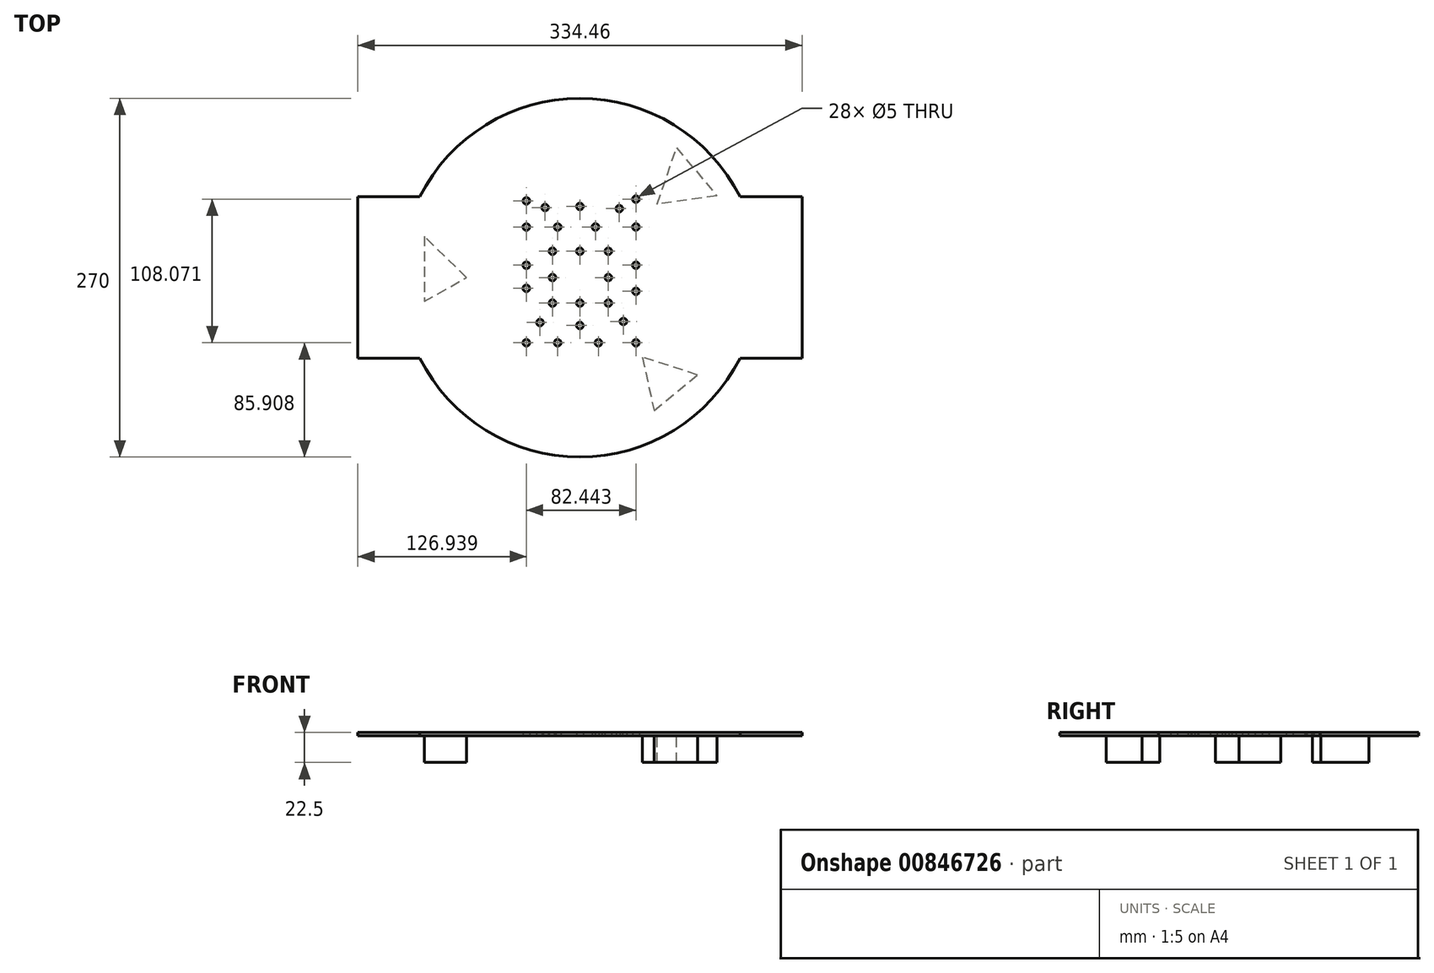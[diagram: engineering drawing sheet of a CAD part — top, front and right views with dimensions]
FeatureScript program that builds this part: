
annotation { "Feature Type Name" : "Feature", "Feature Type Description" : "" }
export const myFeature = defineFeature(function(context is Context, id is Id, definition is map)
    precondition{}
    {
        {
            var Q0;
            Q0=qCreatedBy(makeId("Top.planeOp"),FACE);
            var sketch = newSketch(context, id + "F0", { "sketchPlane" : qUnion([Q0])});
            skCircle(sketch, "E0", {"center": v(0, 0) * mm, "radius": 135 * mm});
            skLineSegment(sketch, "E1.left", {"start": v(167.23, 60.8) * mm, "end": v(167.23, -60.8) * mm});
            skLineSegment(sketch, "E1.right", {"start": v(-167.23, 60.8) * mm, "end": v(-167.23, -60.8) * mm});
            skLineSegment(sketch, "E2", {"start": v(-167.23, 60.8) * mm, "end": v(-120.53, 60.8) * mm});
            skLineSegment(sketch, "E3", {"start": v(120.53, 60.8) * mm, "end": v(167.23, 60.8) * mm});
            skLineSegment(sketch, "E4", {"start": v(-167.23, -60.8) * mm, "end": v(-120.53, -60.8) * mm});
            skLineSegment(sketch, "E5", {"start": v(120.53, -60.8) * mm, "end": v(167.23, -60.8) * mm});
            skPoint(sketch, "E6", {"position": v(0, 19.8) * mm});
            skPoint(sketch, "E7", {"position": v(0, -19.21) * mm});
            skPoint(sketch, "E8", {"position": v(21.4, 0) * mm});
            skPoint(sketch, "E9", {"position": v(-20.65, 0) * mm});
            skPoint(sketch, "E10", {"position": v(-20.65, 19.8) * mm});
            skPoint(sketch, "E11", {"position": v(21.4, 19.8) * mm});
            skPoint(sketch, "E12", {"position": v(21.4, -19.21) * mm});
            skPoint(sketch, "E13", {"position": v(-20.65, -19.21) * mm});
            skPoint(sketch, "E14", {"position": v(-16.78, -49.1) * mm});
            skPoint(sketch, "E15", {"position": v(13.93, -49.1) * mm});
            skPoint(sketch, "E16", {"position": v(11.72, 38.05) * mm});
            skPoint(sketch, "E17", {"position": v(-16.78, 38.05) * mm});
            skPoint(sketch, "E18", {"position": v(42.15, 9.28) * mm});
            skPoint(sketch, "E19", {"position": v(42.15, -10.36) * mm});
            skPoint(sketch, "E20", {"position": v(-40.3, -8.15) * mm});
            skPoint(sketch, "E21", {"position": v(-40.3, 9.28) * mm});
            skPoint(sketch, "E22", {"position": v(-40.3, 38.05) * mm});
            skPoint(sketch, "E23", {"position": v(42.15, 38.05) * mm});
            skPoint(sketch, "E24", {"position": v(42.15, -49.1) * mm});
            skPoint(sketch, "E25", {"position": v(-40.3, -49.1) * mm});
            skPoint(sketch, "E26", {"position": v(0, -36.09) * mm});
            skPoint(sketch, "E27", {"position": v(-30.05, -33.88) * mm});
            skPoint(sketch, "E28", {"position": v(32.75, -33.05) * mm});
            skPoint(sketch, "E29", {"position": v(-26.18, 52.72) * mm});
            skPoint(sketch, "E30", {"position": v(0, 53.55) * mm});
            skPoint(sketch, "E31", {"position": v(29.7, 51.89) * mm});
            skPoint(sketch, "E32", {"position": v(-40.3, 57.7) * mm});
            skPoint(sketch, "E33", {"position": v(42.15, 58.98) * mm});
            skLineSegment(sketch, "E34", {"start": v(-117.25, 31.13) * mm, "end": v(-117.25, -17.96) * mm});
            skLineSegment(sketch, "E35", {"start": v(-117.25, -17.96) * mm, "end": v(-85.33, 0) * mm});
            skLineSegment(sketch, "E36", {"start": v(-85.33, 0) * mm, "end": v(-117.25, 31.13) * mm});
            skLineSegment(sketch, "E37", {"start": v(72.76, 97.7) * mm, "end": v(103.14, 61.47) * mm});
            skLineSegment(sketch, "E38", {"start": v(103.14, 61.47) * mm, "end": v(58.2, 55.23) * mm});
            skLineSegment(sketch, "E39", {"start": v(58.2, 55.23) * mm, "end": v(72.76, 97.7) * mm});
            skLineSegment(sketch, "E40", {"start": v(55.9, -100.06) * mm, "end": v(88.54, -73.28) * mm});
            skLineSegment(sketch, "E41", {"start": v(88.54, -73.28) * mm, "end": v(46.94, -59.96) * mm});
            skLineSegment(sketch, "E42", {"start": v(46.94, -59.96) * mm, "end": v(55.9, -100.06) * mm});
            skSolve(sketch);
        }
        {
            var Q0;
            {var subQ0=sQuery(id+"F0.wireOp",EDGE,"E0");var subQ1=makeQuery(id+"F0.imprint","INTERSECT",VERTEX,{"derivedFrom":[subQ0,sQuery(id+"F0.wireOp",EDGE,"E2")]});Q0=makeQuery(id+"F0.imprint","IMPRINT",FACE,{"disambiguationData":[TD([[makeQuery(id+"F0.imprint","IMPRINT",EDGE,{"disambiguationData":[TD([[subQ1,1.0]])],"derivedFrom":subQ0}),1.0]])]});}
            var Q1;
            Q1=makeQuery(id+"F0.imprint","IMPRINT",FACE,{"disambiguationData":[TD([[makeQuery(id+"F0.imprint","IMPRINT",EDGE,{"derivedFrom":sQuery(id+"F0.wireOp",EDGE,"E1.right")}),1.0]])]});
            var Q2;
            Q2=makeQuery(id+"F0.imprint","IMPRINT",FACE,{"disambiguationData":[TD([[makeQuery(id+"F0.imprint","IMPRINT",EDGE,{"derivedFrom":sQuery(id+"F0.wireOp",EDGE,"E1.left")}),-1.0]])]});
            var Q3;
            {var subQ0=sQuery(id+"F0.wireOp",EDGE,"KSSbLjsO-GVq9-oAiS-ih5v-jaDQlpPfr1M6");Q3=makeQuery(id+"F0.imprint","IMPRINT",FACE,{"disambiguationData":[TD([[makeQuery(id+"F0.imprint","IMPRINT",EDGE,{"derivedFrom":subQ0}),-1.0]])]});}
            var Q4;
            {var subQ0=sQuery(id+"F0.wireOp",EDGE,"6y2jmlKQ-SfiU-YnZR-oIez-cIPMSW9u3y5p");Q4=makeQuery(id+"F0.imprint","IMPRINT",FACE,{"disambiguationData":[TD([[makeQuery(id+"F0.imprint","IMPRINT",EDGE,{"derivedFrom":subQ0}),1.0]])]});}
            var Q5;
            {var subQ0=sQuery(id+"F0.wireOp",EDGE,"5wtv1OCd-jvl7-qsIo-Mp1C-oISwUdbHLiSj");Q5=makeQuery(id+"F0.imprint","IMPRINT",FACE,{"disambiguationData":[TD([[makeQuery(id+"F0.imprint","IMPRINT",EDGE,{"derivedFrom":subQ0}),-1.0]])]});}
            var Q6;
            Q6=makeQuery(id+"F0.imprint","IMPRINT",FACE,{"disambiguationData":[TD([[makeQuery(id+"F0.imprint","IMPRINT",EDGE,{"derivedFrom":sQuery(id+"F0.wireOp",EDGE,"E34")}),1.0]])]});
            var Q7;
            Q7=makeQuery(id+"F0.imprint","IMPRINT",FACE,{"disambiguationData":[TD([[makeQuery(id+"F0.imprint","IMPRINT",EDGE,{"derivedFrom":sQuery(id+"F0.wireOp",EDGE,"E37")}),-1.0]])]});
            var Q8;
            Q8=makeQuery(id+"F0.imprint","IMPRINT",FACE,{"disambiguationData":[TD([[makeQuery(id+"F0.imprint","IMPRINT",EDGE,{"derivedFrom":sQuery(id+"F0.wireOp",EDGE,"E40")}),1.0]])]});
            extrude(context, id + "F1", {"entities" : qUnion([Q0, Q1, Q2, Q3, Q4, Q5, Q6, Q7, Q8]), "depth" : 2.5 * mm, "offsetDistance" : 25.4 * mm});
        }
        {
            var Q0;
            Q0=makeQuery(id+"F0.imprint","IMPRINT",FACE,{"disambiguationData":[TD([[makeQuery(id+"F0.imprint","IMPRINT",EDGE,{"derivedFrom":sQuery(id+"F0.wireOp",EDGE,"E34")}),1.0]])]});
            var Q1;
            Q1=makeQuery(id+"F0.imprint","IMPRINT",FACE,{"disambiguationData":[TD([[makeQuery(id+"F0.imprint","IMPRINT",EDGE,{"derivedFrom":sQuery(id+"F0.wireOp",EDGE,"E37")}),-1.0]])]});
            var Q2;
            Q2=makeQuery(id+"F0.imprint","IMPRINT",FACE,{"disambiguationData":[TD([[makeQuery(id+"F0.imprint","IMPRINT",EDGE,{"derivedFrom":sQuery(id+"F0.wireOp",EDGE,"E40")}),1.0]])]});
            extrude(context, id + "F2", {"entities" : qUnion([Q0, Q1, Q2]), "oppositeDirection" : true, "depth" : 20 * mm, "offsetDistance" : 25.4 * mm});
        }
        {
            var Q0;
            Q0=sQuery(id+"F0.wireOp",VERTEX,"E32");
            var Q1;
            Q1=sQuery(id+"F0.wireOp",VERTEX,"E22");
            var Q2;
            Q2=sQuery(id+"F0.wireOp",VERTEX,"E21");
            var Q3;
            Q3=sQuery(id+"F0.wireOp",VERTEX,"E20");
            var Q4;
            Q4=sQuery(id+"F0.wireOp",VERTEX,"E25");
            var Q5;
            Q5=sQuery(id+"F0.wireOp",VERTEX,"E27");
            var Q6;
            Q6=sQuery(id+"F0.wireOp",VERTEX,"E14");
            var Q7;
            Q7=sQuery(id+"F0.wireOp",VERTEX,"E13");
            var Q8;
            Q8=sQuery(id+"F0.wireOp",VERTEX,"E9");
            var Q9;
            Q9=sQuery(id+"F0.wireOp",VERTEX,"E10");
            var Q10;
            Q10=sQuery(id+"F0.wireOp",VERTEX,"E17");
            var Q11;
            Q11=sQuery(id+"F0.wireOp",VERTEX,"E29");
            var Q12;
            Q12=sQuery(id+"F0.wireOp",VERTEX,"E30");
            var Q13;
            Q13=sQuery(id+"F0.wireOp",VERTEX,"E16");
            var Q14;
            Q14=sQuery(id+"F0.wireOp",VERTEX,"E6");
            var Q15;
            Q15=sQuery(id+"F0.wireOp",VERTEX,"E7");
            var Q16;
            Q16=sQuery(id+"F0.wireOp",VERTEX,"E26");
            var Q17;
            Q17=sQuery(id+"F0.wireOp",VERTEX,"E15");
            var Q18;
            Q18=sQuery(id+"F0.wireOp",VERTEX,"E24");
            var Q19;
            Q19=sQuery(id+"F0.wireOp",VERTEX,"E28");
            var Q20;
            Q20=sQuery(id+"F0.wireOp",VERTEX,"E12");
            var Q21;
            Q21=sQuery(id+"F0.wireOp",VERTEX,"E8");
            var Q22;
            Q22=sQuery(id+"F0.wireOp",VERTEX,"E11");
            var Q23;
            Q23=sQuery(id+"F0.wireOp",VERTEX,"E31");
            var Q24;
            Q24=sQuery(id+"F0.wireOp",VERTEX,"E33");
            var Q25;
            Q25=sQuery(id+"F0.wireOp",VERTEX,"E23");
            var Q26;
            Q26=sQuery(id+"F0.wireOp",VERTEX,"E18");
            var Q27;
            Q27=sQuery(id+"F0.wireOp",VERTEX,"E19");
            var Q28;
            Q28=makeQuery(id+"F1.opExtrude","SWEPT_BODY",BODY,{"disambiguationData":[OSD([sQuery(id+"F0.wireOp",EDGE,"E0"),sQuery(id+"F0.wireOp",EDGE,"E1.left"),sQuery(id+"F0.wireOp",EDGE,"E1.right"),sQuery(id+"F0.wireOp",EDGE,"E2"),sQuery(id+"F0.wireOp",EDGE,"E3"),sQuery(id+"F0.wireOp",EDGE,"E4"),sQuery(id+"F0.wireOp",EDGE,"E5"),sQuery(id+"F0.wireOp",EDGE,"5wtv1OCd-jvl7-qsIo-Mp1C-oISwUdbHLiSj"),sQuery(id+"F0.wireOp",EDGE,"LmDuyGZc-YayC-Vc1Z-F4np-XG6or76GWZyW"),sQuery(id+"F0.wireOp",EDGE,"jy3dwxA2-uTnb-vJjc-XlCD-wZdA5i3FVw9v"),sQuery(id+"F0.wireOp",EDGE,"H1gzx8ib-XVas-nEdD-tjce-u9CqkxxwPEbq"),sQuery(id+"F0.wireOp",EDGE,"R3a1GwYV-HSFf-DV2y-Deem-zfVxDUYStoiJ"),sQuery(id+"F0.wireOp",EDGE,"RzJYX33y-Cw7O-AjXi-TOZJ-VfaitWk6rF7Y"),sQuery(id+"F0.wireOp",EDGE,"veK3jYyw-JbM9-1OWB-acQT-Zl6Bkqya9Qqf")])]});
            hole(context, id + "F3", {"style" : HoleStyle.SIMPLE, "endStyle" : HoleEndStyle.BLIND, "oppositeDirection" : true, "holeDiameter" : 5 * mm, "majorDiameter" : 6.35 * mm, "holeDepth" : 200 * mm, "isTappedThrough" : true, "tappedDepth" : 12.7 * mm, "tapClearance" : 3, "locations" : qUnion([Q0, Q1, Q2, Q3, Q4, Q5, Q6, Q7, Q8, Q9, Q10, Q11, Q12, Q13, Q14, Q15, Q16, Q17, Q18, Q19, Q20, Q21, Q22, Q23, Q24, Q25, Q26, Q27]), "scope" : qUnion([Q28])});
        }
    });
